# Revit family: LAMP_LAMPTUB LED
name_source: partatom
category: Modelos genéricos
revit_build: Autodesk Revit 2015 (Build: 20140606_1530(x64)
units: mm (PartAtom-declared; Revit-internal decimal feet)

## types (8) — shared parameters
CRI = 80
Comentarios de tipo = Availability of switching between accessories through visibility parameters when placed in a project.
Diameter = 80 mm  [stored 0.262467 ft]
Elevación por defecto = 1219 mm
Fabricante = LAMP
Finish = Shiny white
Gear = Electronic
IEE = A++
Installation instructions = https://www.lamp.es
Insulation class = I
LED Lifetime = 50.000 L80 B10
Lamp = MID-POWER LED
Last update = 30/09/2020
Long. suspensión = 484 mm  [stored 1.58793 ft]
Luminaire type = Indoor - Modular Systems
MacAdam = 3
Manufacturer URL = http://www.lamp.es
Manufacturer country = Spain
Manufacturer name = LAMP
Model explanation = Availability of switching between accessories through visibility parameters when placed in a project.
Photometric web file = Cuerpo Lamptub : 2278LM 3000 1162MM
Power Supply = 220-240V 50-60Hz
Product URL = https://www.lamp.es
Product datasheet = http://www.lamp.es
Protection rating = IP20
Type = MID POWER PHILIPS

## per-type parameters (varying)
| type | Descripción | Efficacy | Initial color | Initial intensity | Modelo | Plum | Power | Product code | Weight |
| 2278LM 3000 1162MM | LAMPTUB LED OPAL SUS 2600 WW WH. | 119 lm/W | 3000 K | 2278 lm | LA1SF120LOOP830NW | 19 W | 17 W | LA1SF120LOOP830NW | 2.39 kg |
| 2322LM 4000 1162MM | LAMPTUB LED OPAL SUS 2600 NW WH. | 121 lm/W | 4000 K | 2322 lm | LA1SF120LOOP840NW | 19 W | 17 W | LA1SF120LOOP840NW | 2.39 kg |
| 3601LM 3000 1162MM | LAMPTUB LED OPAL SUS 3900 WW WH. | 121 lm/W | 3000 K | 3601 lm | LA1SF170LOOP830NW | 30 W | 25 W | LA1SF170LOOP830NW | 3.61 kg |
| 3683LM 4000 1162MM | LAMPTUB LED OPAL SUS 3900 NW WH. | 124 lm/W | 4000 K | 3683 lm | LA1SF170LOOP840NW | 30 W | 25 W | LA1SF170LOOP840NW | 3.61 kg |
| 3896LM 3000 1743MM | LAMPTUB LED OPAL SUS 4400 WW WH. | 127 lm/W | 3000 K | 3896 lm | LA1SF120MOOP830NW | 31 W | 28 W | LA1SF120MOOP830NW | 2.39 kg |
| 3986LM 4000 1743MM | LAMPTUB LED OPAL SUS 4400 NW WH. | 130 lm/W | 4000 K | 3986 lm | LA1SF120MOOP840NW | 31 W | 28 W | LA1SF120MOOP840NW | 2.39 kg |
| 6161LM 3000 1743MM | LAMPTUB LED OPAL SUS 6600 WW WH. | 135 lm/W | 3000 K | 6161 lm | LA1SF170MOOP830NW | 46 W | 41 W | LA1SF170MOOP830NW | 3.61 kg |
| 6299LM 4000 1743MM | LAMPTUB LED OPAL SUS 6600 NW WH. | 138 lm/W | 4000 K | 6299 lm | LA1SF170MOOP840NW | 46 W | 41 W | LA1SF170MOOP840NW | 3.61 kg |

note: [stored X ft] marks values corroborated as IEEE doubles in the binary element streams (Revit-internal decimal feet)
